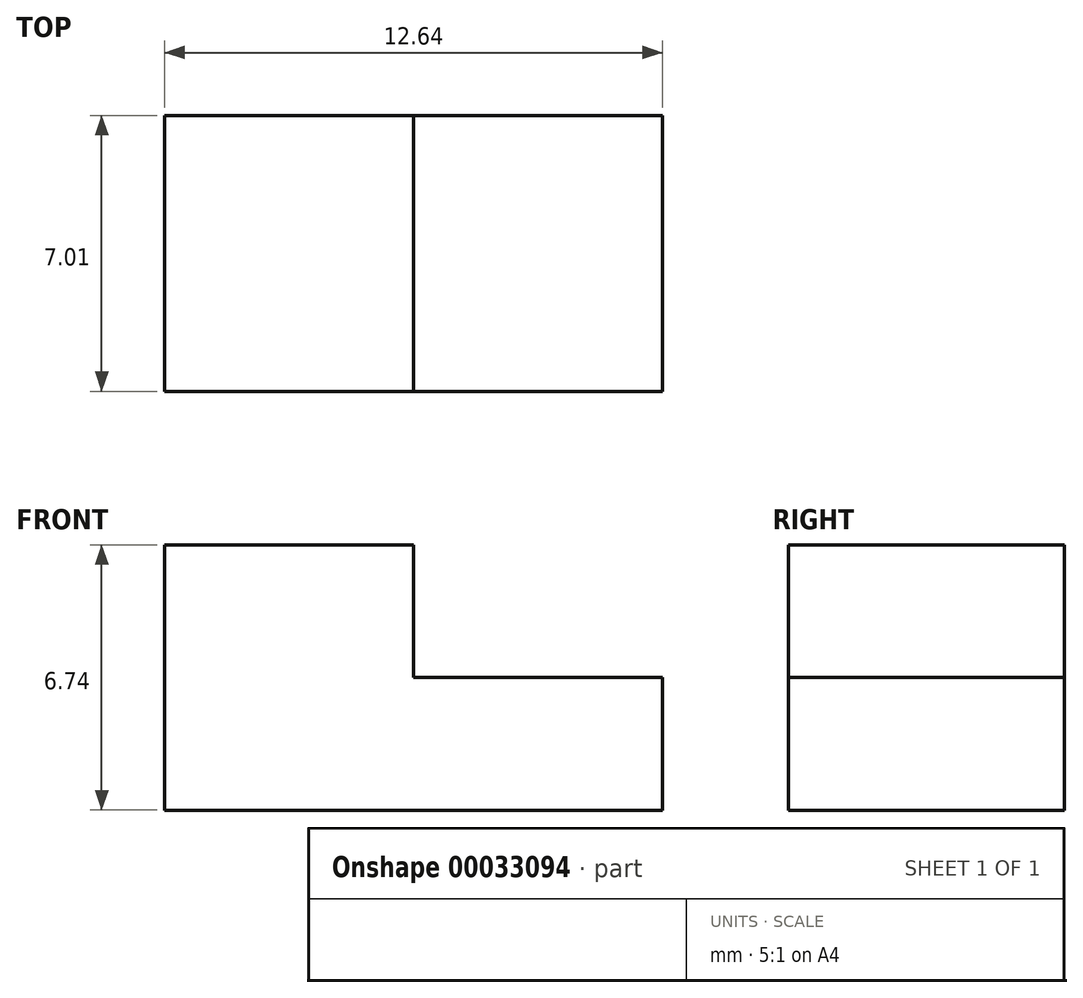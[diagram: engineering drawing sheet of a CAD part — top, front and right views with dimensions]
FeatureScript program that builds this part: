
annotation { "Feature Type Name" : "Feature", "Feature Type Description" : "" }
export const myFeature = defineFeature(function(context is Context, id is Id, definition is map)
    precondition{}
    {
        {
            var Q0;
            Q0=qCreatedBy(makeId("Front.planeOp"),FACE);
            var sketch = newSketch(context, id + "F0", { "sketchPlane" : qUnion([Q0])});
            skLineSegment(sketch, "E0.rect.bottom", {"start": v(6.32, -3.37) * mm, "end": v(-6.32, -3.37) * mm});
            skLineSegment(sketch, "E0.rect.top", {"start": v(0, 3.37) * mm, "end": v(-6.32, 3.37) * mm});
            skLineSegment(sketch, "E0.rect.left", {"start": v(6.32, -3.37) * mm, "end": v(6.32, 0) * mm});
            skLineSegment(sketch, "E0.rect.right", {"start": v(-6.32, -3.37) * mm, "end": v(-6.32, 3.37) * mm});
            skPoint(sketch, "E0.rect.middle", {"position": v(0, 0) * mm});
            skLineSegment(sketch, "E1.top", {"start": v(6.32, 0) * mm, "end": v(0, 0) * mm});
            skLineSegment(sketch, "E1.right", {"start": v(0, 3.37) * mm, "end": v(0, 0) * mm});
            skPoint(sketch, "E2.orphan", {"position": v(6.32, 3.37) * mm});
            skSolve(sketch);
        }
        {
            var Q0;
            Q0 = qSketchRegion(id + "F0", true);
            extrude(context, id + "F1", {"entities" : qUnion([Q0]), "depth" : 7 * mm});
        }
    });
